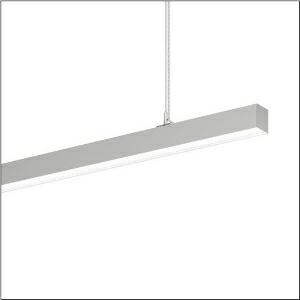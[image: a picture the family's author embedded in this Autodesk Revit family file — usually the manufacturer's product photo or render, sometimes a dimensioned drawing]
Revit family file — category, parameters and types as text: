
# Revit family: silica_21_51mx33dc3dsb
name_source: partatom
category: Lighting Fixtures
units: mm (PartAtom-declared; Revit-internal decimal feet)

## family parameters
Cut with Voids When Loaded = No
Host = Face
Light Source = No
Part Type = Normal
Room Calculation Point = No
Round Connector Dimension = Use Diameter
Shared = No

## types (1)
- --- (1 x LED, 14780 lm, 99.5 W, 3000K)
    Apparent Load = 100 VA
    CIE Flux Codes = 78 96 99 55 100
    Color Rendering = 80
    Color Temperature = 3000K
    Default Elevation = 1800 mm
    Description = Silica 21, office luminaire, primary optical cover: prismatic diffuser, of PMMA, CAT 2 (L<= 3000cd/m²), light emission: direct/indirect distribution, primary light characteristic: symmetric, installation type: suspended mounting, LED, rated luminous flux: 14.780lm, luminous efficacy: 149lm/W, light colour: 830, colour temperature: 3000K, control gear: DALI 2, with terminal, 3+2-pole, max. 2.5mm², mains connection: 220..240V, AC, 50/60Hz, rated input power: 99.5W, luminaire housing, of aluminium, metallic grey (RAL 9006), length: 3.004mm, width: 53mm, height: 53mm, protection rating (complete): IP20, insulation class (complete): insulation class I (protective earthing), certification: CE, permissible operating ambient temperature: 0..+35°C, standard: EN 50419, packaging unit: 1 piece
    Height = 53 mm
    Lamp = 1 x LED
    Lamp Light Flux = 14780 lm
    Lamp Power = 99.5 W
    Lamp count = 1
    Length = 3004 mm
    Luminous efficacy = 149 lm/W
    Manufacturer = Siteco
    ModVariant = No
    Model = 51MX33DC3DSB
    Mounting Place = Ceiling
    Mounting Type = Pendant
    Number of Poles = 1
    OnlyDefault = Yes
    Power Factor = 1
    Product Name = Silica 21
    Product group = office luminaire | ceiling pendant
    ProductGroupID = 903
    Protection Class = Protection class I
    Protection Degree = IP 20
    RLX_Detail_Level = 1
    RLX_Emergency_Light_Flux = 0 lm
    RLX_Emergency_Type = 0
    RLX_Emergency_Type_DB = No
    RlxData = <blob elided: 23437 chars, md5=7100ce71>
    Socket = socket
    Standby Power = 0 W
    System Light Flux = 14780 lm
    System Power = 100 W
    Type Comments = factory setting: luminous flux: 100 % | dim-lin: 254 | 345 mA
    Type Image = l_1335864.jpg
    URL = http://relux.com
    VarID = @adj_118629
    Voltage = 0 V
    Weight = 0.00 kg
    Width = 53 mm

## geometry (parser evidence)
native form markers: Blend x4, Sweep x11
no freeform markers — native parametric forms only
